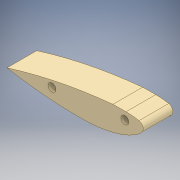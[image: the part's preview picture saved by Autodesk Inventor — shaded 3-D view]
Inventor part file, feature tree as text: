
AUTODESK INVENTOR PART (.ipt)
format: ipt  version: 2018 (Build 220112000, 112)  size: 120,832 bytes
history: native  units: mm
features: extrude x1, sketch x1, projected_geometry x1
ambient origin geometry x8: Origin, YZ Plane, XZ Plane, XY Plane, X Axis, Y Axis, Z Axis, Center Point
bodies: Body1 (feature_tree)
feature tree (3):
  extrude  "押し出し2"  Depth=44.75mm TaperAngle=0.0deg
  sketch  "スケッチ1"
  projected_geometry  "投影ループ1"
